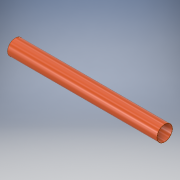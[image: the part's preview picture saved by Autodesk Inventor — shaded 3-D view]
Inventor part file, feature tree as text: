
AUTODESK INVENTOR PART (.ipt)
format: ipt  version: 2017 SP1 (Build 210196100, 196)  size: 102,400 bytes
history: native  units: in
note: dims shown in document units (in); Inventor stores cm internally (conversion verified against a paired STEP export)
features: revolve x1, shell x1, sketch x1
ambient origin geometry x8: Origin, YZ Plane, XZ Plane, XY Plane, X Axis, Y Axis, Z Axis, Center Point
bodies: Solid1 (feature_tree)
feature tree (3):
  revolve  "Revolution1"  [1 undecoded]
  shell  "Shell1"  Thickness=90.0deg
  sketch  "Sketch1"  dims[d0=72.0in d1=3.75in d2=90.0deg d3=0.125in]
note: 1 required parameter value undecoded (feature->parameter linkage not recoverable at this tier; creation-order binding heuristic only, values carry confidence <= 0.55)
